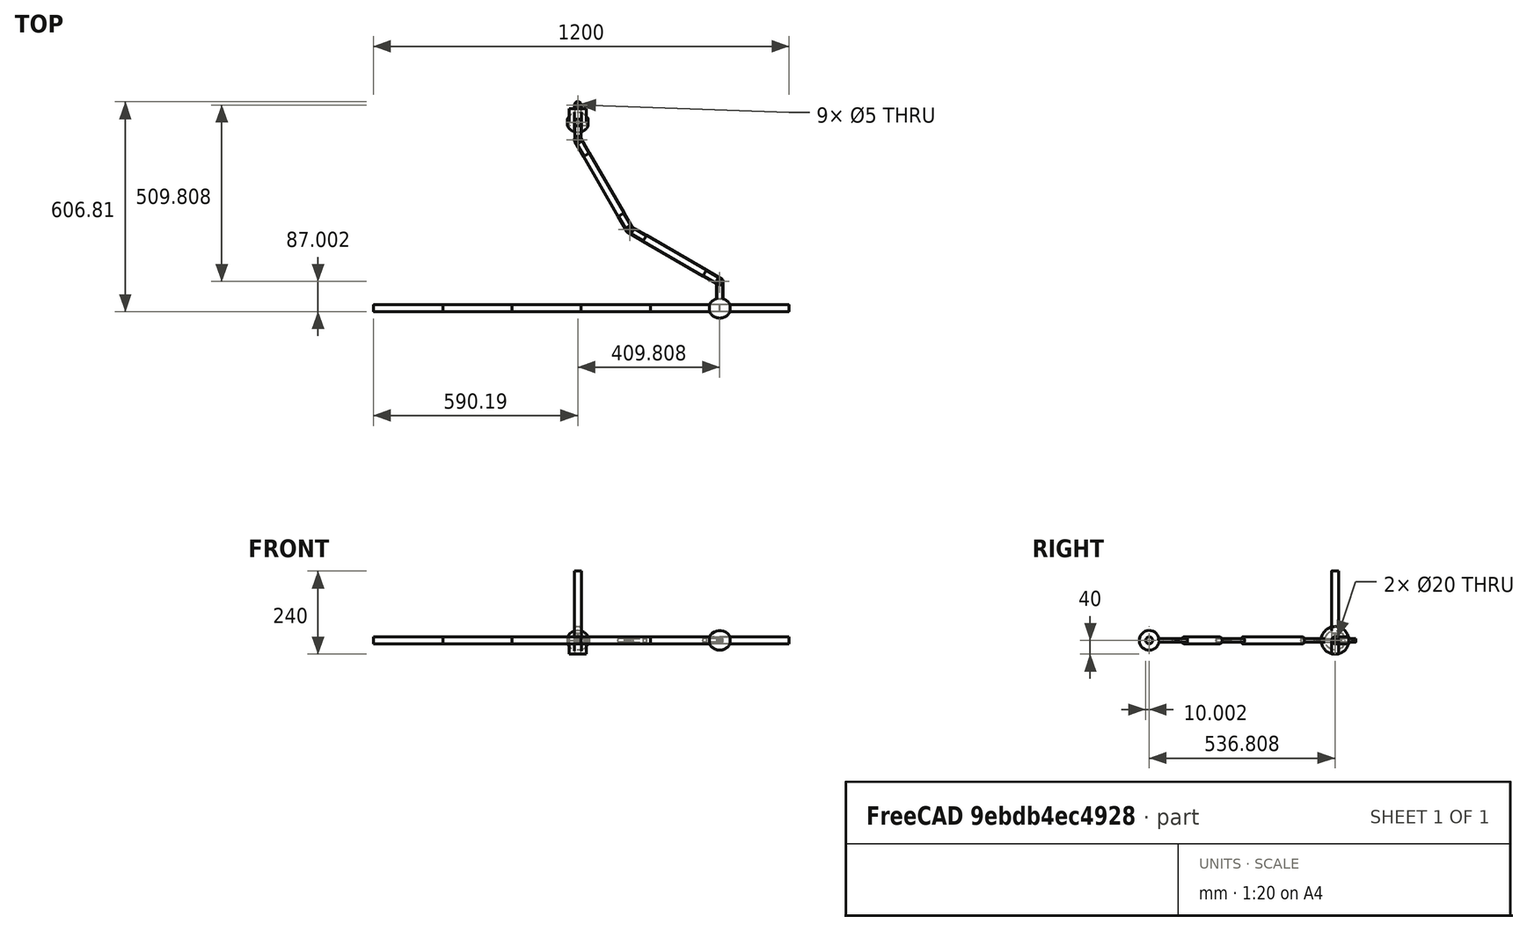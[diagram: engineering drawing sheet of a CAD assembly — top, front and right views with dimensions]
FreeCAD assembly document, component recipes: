
FREECAD ASSEMBLY — COMPONENT RECIPES ("Demo5Rev-Rev-Rev")

This assembly document has 7 components, labeled P0..P6 below (a component is one placed body or linked part). 7 of them carry a construction recipe — the FreeCAD feature program that regenerates the part from scratch, quoted from this document or its linked companion documents; the rest are supplied as boundary geometry only. No exploded tour is included for this assembly.
COMPONENT P0 — recipe-attached ("Weight", modeled in this document).
Construction recipe (the document's own serialized feature program — sketch geometry with constraints, then the solid features built on it; lengths are millimeters unless a unit is written):

FEATURE [Sketcher::SketchObject] Sketch
  FullyConstrained = true
  MapMode = 5
  Support = -> [XY_Plane]
  sketch-geometry (2):
    g0: LineSegment StartX=-30 StartY=10 StartZ=0 EndX=30 EndY=10 EndZ=0
    g1: ArcOfCircle CenterX=0 CenterY=-5 CenterZ=0 NormalX=0 NormalY=0 NormalZ=1 AngleXU=0 Radius=33.541 StartAngle=0.463648 EndAngle=2.67795
  constraints (7):
    c: Horizontal(g0)
    c: DistanceY(g-1,g0) = 10
    c: DistanceX(g-1,g0) = 30
    c: PointOnObject(g1,g-2)
    c: DistanceY(g1,g-1) = 5
    c: Coincident(g1,g0)
    c: Coincident(g1,g0)
FEATURE [PartDesign::Revolution] Revolution
  Angle = 360
  Axis = (1,0,0)
  Base = (0,0,0)
  Profile = -> Sketch
  ReferenceAxis = -> Sketch [H_Axis]
FEATURE [PartDesign::CoordinateSystem] WeightTop
  AttacherType = Attacher::AttachEngine3D
  MapMode = 11
  Placement = pos=(30,-1.8e-15,0) rot=(0.707107,0,0.707107;3.14159rad)
  Support = -> [Revolution]
FEATURE [PartDesign::CoordinateSystem] WeightBot
  AttacherType = Attacher::AttachEngine3D
  MapMode = 11
  Placement = pos=(-30,0,0) rot=(0.707107,0,0.707107;3.14159rad)
  Support = -> [Revolution]
FEATURE [PartDesign::CoordinateSystem] WeightLCS
  AttacherType = Attacher::AttachEngine3D
  MapMode = 2
  Support = -> [Body003]
FEATURE [PartDesign::Body] Body  label="Weight"
  Group = -> [Sketch,Revolution,WeightLCS,WeightTop,WeightBot]
  Origin = -> Origin
  Tip = -> Revolution
COMPONENT P1 — recipe-attached ("Rod", modeled in this document).
Construction recipe (the document's own serialized feature program — sketch geometry with constraints, then the solid features built on it; lengths are millimeters unless a unit is written):

FEATURE [Sketcher::SketchObject] Sketch001
  FullyConstrained = true
  MapMode = 5
  Support = -> [XY_Plane001]
  sketch-geometry (1):
    g0: Circle CenterX=0 CenterY=0 CenterZ=0 NormalX=0 NormalY=0 NormalZ=1 AngleXU=0 Radius=10
  constraints (2):
    c: Coincident(g0,g-1)
    c: Diameter(g0) = 20
FEATURE [PartDesign::Pad] Pad
  Direction = (0,0,1)
  Length = 200
  Length2 = 10
  Profile = -> Sketch001
  ReferenceAxis = -> Sketch001 [N_Axis]
  Type = 0
FEATURE [PartDesign::CoordinateSystem] RodTop
  AttacherType = Attacher::AttachEngine3D
  MapMode = 11
  Placement = pos=(0,0,200) rot=(0,0,1;1.5708rad)
  Support = -> [Pad]
FEATURE [PartDesign::CoordinateSystem] RodBottom
  AttacherType = Attacher::AttachEngine3D
  MapMode = 11
  Placement = pos=(0,0,0) rot=(0,0,1;1.5708rad)
  Support = -> [Pad]
FEATURE [PartDesign::Body] Body001  label="Rod"
  Group = -> [Sketch001,Pad,RodTop,RodBottom]
  Origin = -> Origin001
  Tip = -> Pad
COMPONENT P2 — recipe-attached ("LugBody", modeled in this document).
Construction recipe (the document's own serialized feature program — sketch geometry with constraints, then the solid features built on it; lengths are millimeters unless a unit is written):

FEATURE [Sketcher::SketchObject] Sketch002
  FullyConstrained = true
  MapMode = 5
  Support = -> [XY_Plane002]
  sketch-geometry (5):
    g0: LineSegment StartX=-10 StartY=0 StartZ=0 EndX=-10 EndY=50 EndZ=0
    g1: ArcOfCircle CenterX=0 CenterY=50 CenterZ=0 NormalX=0 NormalY=0 NormalZ=1 AngleXU=0 Radius=10 StartAngle=1e-16 EndAngle=3.14159
    g2: LineSegment StartX=10 StartY=50 StartZ=0 EndX=10 EndY=0 EndZ=0
    g3: LineSegment StartX=10 StartY=0 StartZ=0 EndX=-10 EndY=0 EndZ=0
    g4: Circle CenterX=0 CenterY=50 CenterZ=0 NormalX=0 NormalY=0 NormalZ=1 AngleXU=0 Radius=2.5
  constraints (13):
    c: PointOnObject(g0,g-1)
    c: Vertical(g0)
    c: Tangent(g0,g1) = 1.5708
    c: Tangent(g1,g2) = 1.5708
    c: Coincident(g2,g3)
    c: Coincident(g3,g0)
    c: Horizontal(g3)
    c: PointOnObject(g1,g-2)
    c: Vertical(g2)
    c: Diameter(g1) = 20
    c: Distance(g2) = 50
    c: Coincident(g4,g1)
    c: Diameter(g4) = 5
FEATURE [PartDesign::Pad] Pad001
  Direction = (0,0,1)
  Length = 10
  Length2 = 10
  Midplane = true
  Profile = -> Sketch002
  ReferenceAxis = -> Sketch002 [N_Axis]
  Type = 0
FEATURE [PartDesign::Body] Body002  label="LugBody"
  Group = -> [Sketch002,Pad001]
  Origin = -> Origin002
  Tip = -> Pad001
COMPONENT P3 — recipe-attached ("LugCylinder", modeled in this document).
Construction recipe (the document's own serialized feature program — sketch geometry with constraints, then the solid features built on it; lengths are millimeters unless a unit is written):

FEATURE [Sketcher::SketchObject] Sketch003
  FullyConstrained = true
  MapMode = 5
  Placement = pos=(0,0,0) rot=(1,0,0;1.5708rad)
  Support = -> [XZ_Plane003]
  sketch-geometry (1):
    g0: Circle CenterX=0 CenterY=0 CenterZ=0 NormalX=0 NormalY=0 NormalZ=1 AngleXU=0 Radius=10
  constraints (2):
    c: Coincident(g0,g-1)
    c: Diameter(g0) = 20
FEATURE [PartDesign::Pad] Pad002
  Direction = (0,-1,-2e-16)
  Length = 60
  Length2 = 10
  Placement = pos=(0,0,0) rot=(1,0,0;1.5708rad)
  Profile = -> Sketch003
  ReferenceAxis = -> Sketch003 [N_Axis]
  Reversed = true
  Type = 0
FEATURE [PartDesign::Boolean] Boolean
  BaseFeature = -> Pad002
  Group = -> [Body002]
  Type = 2
FEATURE [PartDesign::CoordinateSystem] LugHole
  AttacherType = Attacher::AttachEngine3D
  MapMode = 11
  Placement = pos=(0,50,5) rot=(0,0,1;1.5708rad)
  Support = -> [Boolean]
FEATURE [PartDesign::CoordinateSystem] LugFace
  AttacherType = Attacher::AttachEngine3D
  MapMode = 5
  Placement = pos=(0,0,0) rot=(1,0,0;1.5708rad)
  Support = -> [Boolean]
FEATURE [PartDesign::CoordinateSystem] LugRot30
  AttacherType = Attacher::AttachEngine3D
  AttachmentOffset = pos=(0,0,0) rot=(0,0,1;0.523599rad)
  MapMode = 11
  Placement = pos=(0,50,5) rot=(0,0,1;2.0944rad)
  Support = -> [Boolean]
FEATURE [PartDesign::CoordinateSystem] LugRot60
  AttacherType = Attacher::AttachEngine3D
  AttachmentOffset = pos=(0,0,0) rot=(0,0,1;1.0472rad)
  MapMode = 11
  Placement = pos=(0,50,5) rot=(0,0,1;2.61799rad)
  Support = -> [Boolean]
FEATURE [PartDesign::Body] Body003  label="LugCylinder"
  Group = -> [Sketch003,Pad002,Boolean,LugHole,LugFace,LugRot30,LugRot60]
  Origin = -> Origin003
  Tip = -> Boolean
COMPONENT P4 — recipe-attached ("BobBody", modeled in this document).
Construction recipe (the document's own serialized feature program — sketch geometry with constraints, then the solid features built on it; lengths are millimeters unless a unit is written):

FEATURE [Sketcher::SketchObject] Sketch004
  FullyConstrained = true
  MapMode = 5
  Support = -> [XY_Plane004]
  sketch-geometry (4):
    g0: LineSegment StartX=-10 StartY=0 StartZ=0 EndX=-10 EndY=30 EndZ=0
    g1: ArcOfCircle CenterX=0 CenterY=30 CenterZ=0 NormalX=0 NormalY=0 NormalZ=1 AngleXU=0 Radius=10 StartAngle=2e-16 EndAngle=3.14159
    g2: LineSegment StartX=10 StartY=30 StartZ=0 EndX=10 EndY=0 EndZ=0
    g3: LineSegment StartX=10 StartY=0 StartZ=0 EndX=-10 EndY=0 EndZ=0
  constraints (11):
    c: PointOnObject(g0,g-1)
    c: Vertical(g0)
    c: Tangent(g0,g1) = 1.5708
    c: Tangent(g1,g2) = 1.5708
    c: Coincident(g2,g3)
    c: Coincident(g3,g0)
    c: Vertical(g2)
    c: PointOnObject(g1,g-2)
    c: Diameter(g1) = 20
    c: Distance(g0) = 30
    c: PointOnObject(g2,g-1)
FEATURE [PartDesign::Revolution] Revolution001
  Angle = 360
  Axis = (1,0,0)
  Base = (0,0,0)
  Profile = -> Sketch004
  ReferenceAxis = -> Sketch004 [H_Axis]
FEATURE [PartDesign::CoordinateSystem] BobBody  label="BobBody001"
  AttacherType = Attacher::AttachEngine3D
  MapMode = 11
  Placement = pos=(-10,0,0) rot=(0.707107,0,0.707107;3.14159rad)
  Support = -> [Revolution001]
FEATURE [PartDesign::Body] Body004  label="BobBody"
  Group = -> [Sketch004,Revolution001,BobBody]
  Origin = -> Origin004
  Tip = -> Revolution001
COMPONENT P5 — recipe-attached ("GroundBody", modeled in this document).
Construction recipe (the document's own serialized feature program — sketch geometry with constraints, then the solid features built on it; lengths are millimeters unless a unit is written):

FEATURE [Sketcher::SketchObject] Sketch005
  FullyConstrained = true
  MapMode = 5
  Support = -> [XY_Plane005]
  sketch-geometry (4):
    g0: LineSegment StartX=-25 StartY=10 StartZ=0 EndX=25 EndY=10 EndZ=0
    g1: LineSegment StartX=25 StartY=10 StartZ=0 EndX=25 EndY=-10 EndZ=0
    g2: LineSegment StartX=25 StartY=-10 StartZ=0 EndX=-25 EndY=-10 EndZ=0
    g3: LineSegment StartX=-25 StartY=-10 StartZ=0 EndX=-25 EndY=10 EndZ=0
  constraints (11):
    c: Coincident(g0,g1)
    c: Coincident(g1,g2)
    c: Coincident(g2,g3)
    c: Coincident(g3,g0)
    c: Horizontal(g0)
    c: Horizontal(g2)
    c: Vertical(g1)
    c: Vertical(g3)
    c: DistanceY(g2,g0) = 20
    c: DistanceX(g0,g0) = 50
    c: Symmetric(g0,g1,g-1)
FEATURE [PartDesign::Pad] Pad003
  Direction = (0,0,1)
  Length = 40
  Length2 = 10
  Profile = -> Sketch005
  ReferenceAxis = -> Sketch005 [N_Axis]
  Reversed = true
  Type = 0
FEATURE [PartDesign::CoordinateSystem] GroundLCS
  AttacherType = Attacher::AttachEngine3D
  MapMode = 5
  Placement = pos=(0,0,-40) rot=(1,0,0;3.14159rad)
  Support = -> [Pad003]
FEATURE [PartDesign::Body] Body005  label="GroundBody"
  Group = -> [Sketch005,Pad003,GroundLCS]
  Origin = -> Origin005
  Tip = -> Pad003
COMPONENT P6 — recipe-attached ("Spacer", modeled in this document).
Construction recipe (the document's own serialized feature program — sketch geometry with constraints, then the solid features built on it; lengths are millimeters unless a unit is written):

FEATURE [Sketcher::SketchObject] Sketch006
  FullyConstrained = true
  MapMode = 5
  Support = -> [XY_Plane007]
  sketch-geometry (2):
    g0: Circle CenterX=0 CenterY=0 CenterZ=0 NormalX=0 NormalY=0 NormalZ=1 AngleXU=0 Radius=10
    g1: Circle CenterX=0 CenterY=0 CenterZ=0 NormalX=0 NormalY=0 NormalZ=1 AngleXU=0 Radius=2.5
  constraints (4):
    c: Coincident(g0,g-1)
    c: Coincident(g1,g0)
    c: Diameter(g0) = 20
    c: Diameter(g1) = 5
FEATURE [PartDesign::Pad] Pad004
  Direction = (0,0,1)
  Length = 20
  Length2 = 10
  Profile = -> Sketch006
  ReferenceAxis = -> Sketch006 [N_Axis]
  Type = 0
FEATURE [PartDesign::CoordinateSystem] SpacerTop
  AttacherType = Attacher::AttachEngine3D
  MapMode = 11
  Placement = pos=(0,0,20) rot=(0,0,1;1.5708rad)
  Support = -> [Pad004]
FEATURE [PartDesign::Body] Body006  label="Spacer"
  Group = -> [Sketch006,Pad004,SpacerTop]
  Origin = -> Origin007
  Tip = -> Pad004
PROVENANCE & LICENSES
A FreeCAD (.FCStd) document from a public repository crawl; recipes are the document's own serialized feature recipes (and, for linked parts, companion documents' recipes).
License: gpl-3.0.
